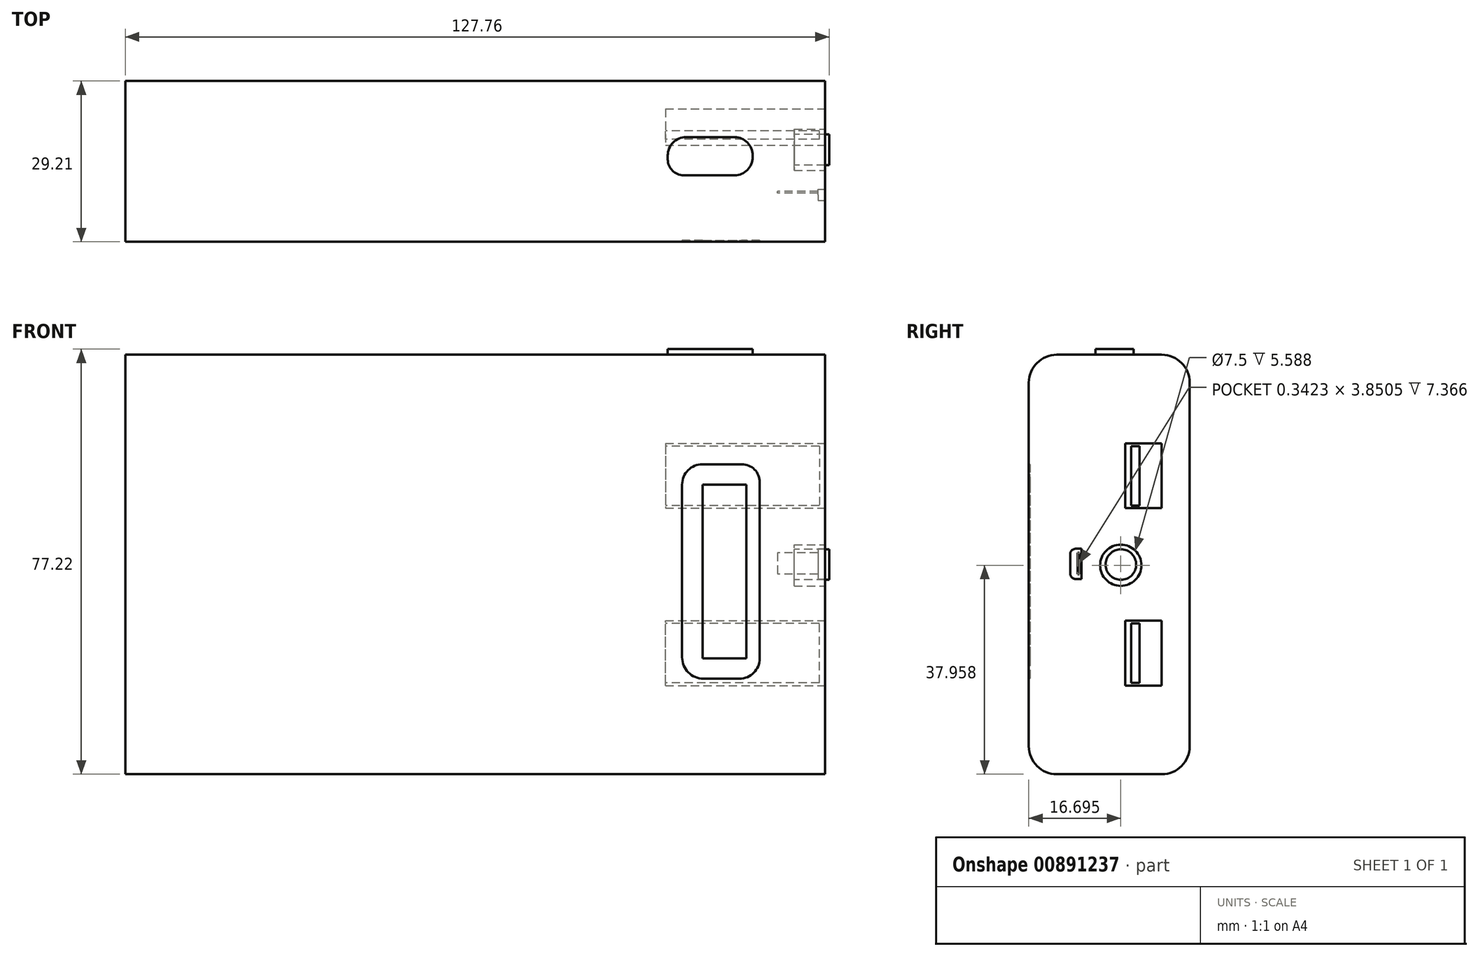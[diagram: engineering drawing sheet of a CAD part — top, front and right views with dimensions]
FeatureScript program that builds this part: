
annotation { "Feature Type Name" : "Feature", "Feature Type Description" : "" }
export const myFeature = defineFeature(function(context is Context, id is Id, definition is map)
    precondition{}
    {
        {
            var Q0;
            Q0=qCreatedBy(makeId("Front.planeOp"),FACE);
            var sketch = newSketch(context, id + "F0", { "sketchPlane" : qUnion([Q0])});
            skLineSegment(sketch, "E0.bottom", {"start": v(-63.5, 38.1) * mm, "end": v(63.5, 38.1) * mm});
            skLineSegment(sketch, "E0.top", {"start": v(-63.5, -38.1) * mm, "end": v(63.5, -38.1) * mm});
            skLineSegment(sketch, "E0.left", {"start": v(-63.5, 38.1) * mm, "end": v(-63.5, -38.1) * mm});
            skLineSegment(sketch, "E0.right", {"start": v(63.5, 38.1) * mm, "end": v(63.5, -38.1) * mm});
            skPoint(sketch, "E0.middle", {"position": v(0, 0) * mm});
            skSolve(sketch);
        }
        {
            var Q0;
            Q0=makeQuery(id+"F0.imprint","IMPRINT",FACE,{"disambiguationData":[TD([[makeQuery(id+"F0.imprint","IMPRINT",EDGE,{"derivedFrom":sQuery(id+"F0.wireOp",EDGE,"E0.bottom")}),-1.0]])]});
            extrude(context, id + "F1", {"entities" : qUnion([Q0]), "depth" : 29.2 * mm, "offsetDistance" : 25.4 * mm});
        }
        {
            var Q0;
            Q0=makeQuery(id+"F1.opExtrude","CAP_EDGE",EDGE,{"disambiguationData":[OSD([sQuery(id+"F0.wireOp",EDGE,"E0.bottom")])],"isStart":false});
            var Q1;
            Q1=makeQuery(id+"F1.opExtrude","CAP_EDGE",EDGE,{"disambiguationData":[OSD([sQuery(id+"F0.wireOp",EDGE,"E0.bottom")])],"isStart":true});
            var Q2;
            Q2=makeQuery(id+"F1.opExtrude","CAP_EDGE",EDGE,{"disambiguationData":[OSD([sQuery(id+"F0.wireOp",EDGE,"E0.top")])],"isStart":false});
            var Q3;
            Q3=makeQuery(id+"F1.opExtrude","CAP_EDGE",EDGE,{"disambiguationData":[OSD([sQuery(id+"F0.wireOp",EDGE,"E0.top")])],"isStart":true});
            fillet(context, id + "F2", {"entities" : qUnion([Q0, Q1, Q2, Q3]), "radius" : 5.08 * mm, "tangentPropagation" : true, "allowEdgeOverflow" : false});
        }
        {
            var Q0;
            Q0=makeQuery(id+"F1.opExtrude","SWEPT_FACE",FACE,{"disambiguationData":[OSD([sQuery(id+"F0.wireOp",EDGE,"E0.right")])]});
            var sketch = newSketch(context, id + "F3", { "sketchPlane" : qUnion([Q0])});
            skLineSegment(sketch, "E1.bottom", {"start": v(-5.08, 22.02) * mm, "end": v(-11.7, 22.02) * mm});
            skLineSegment(sketch, "E1.top", {"start": v(-5.08, 10.22) * mm, "end": v(-11.7, 10.22) * mm});
            skLineSegment(sketch, "E1.left", {"start": v(-5.08, 22.02) * mm, "end": v(-5.08, 10.22) * mm});
            skLineSegment(sketch, "E1.right", {"start": v(-11.7, 22.02) * mm, "end": v(-11.7, 10.22) * mm});
            skLineSegment(sketch, "E2.MirrorCS", {"start": v(-5.08, -22.02) * mm, "end": v(-11.7, -22.02) * mm});
            skLineSegment(sketch, "E3.MirrorCS", {"start": v(-5.08, -22.02) * mm, "end": v(-5.08, -10.22) * mm});
            skLineSegment(sketch, "E4.MirrorCS", {"start": v(-5.08, -10.22) * mm, "end": v(-11.7, -10.22) * mm});
            skLineSegment(sketch, "E5.MirrorCS", {"start": v(-11.7, -22.02) * mm, "end": v(-11.7, -10.22) * mm});
            skSolve(sketch);
        }
        {
            var Q0;
            Q0 = qSketchRegion(id + "F3", true);
            extrude(context, id + "F4", {"entities" : qUnion([Q0]), "operationType" : NewBodyOperationType.REMOVE, "oppositeDirection" : true, "depth" : 28.96 * mm, "offsetDistance" : 25.4 * mm});
        }
        {
            var Q0;
            Q0=makeQuery(id+"F4.boolean.opBoolean","COPY",FACE,{"derivedFrom":makeQuery(id+"F4.opExtrude","CAP_FACE",FACE,{"disambiguationData":[OSD([sQuery(id+"F3.wireOp",EDGE,"E1.bottom"),sQuery(id+"F3.wireOp",EDGE,"E1.top"),sQuery(id+"F3.wireOp",EDGE,"E1.left"),sQuery(id+"F3.wireOp",EDGE,"E1.right")])],"isStart":false})});
            var sketch = newSketch(context, id + "F5", { "sketchPlane" : qUnion([Q0])});
            skLineSegment(sketch, "E6.bottom", {"start": v(-10.61, 21.5) * mm, "end": v(-9.09, 21.5) * mm});
            skLineSegment(sketch, "E6.top", {"start": v(-10.61, 10.68) * mm, "end": v(-9.09, 10.68) * mm});
            skLineSegment(sketch, "E6.left", {"start": v(-10.61, 21.5) * mm, "end": v(-10.61, 10.68) * mm});
            skLineSegment(sketch, "E6.right", {"start": v(-9.09, 21.5) * mm, "end": v(-9.09, 10.68) * mm});
            skLineSegment(sketch, "E7.MirrorCS", {"start": v(-10.61, -21.5) * mm, "end": v(-10.61, -10.68) * mm});
            skLineSegment(sketch, "E8.MirrorCS", {"start": v(-9.09, -21.5) * mm, "end": v(-9.09, -10.68) * mm});
            skLineSegment(sketch, "E9.MirrorCS", {"start": v(-10.61, -10.68) * mm, "end": v(-9.09, -10.68) * mm});
            skLineSegment(sketch, "E10.MirrorCS", {"start": v(-10.61, -21.5) * mm, "end": v(-9.09, -21.5) * mm});
            skSolve(sketch);
        }
        {
            var Q0;
            Q0=makeQuery(id+"F5.imprint","IMPRINT",FACE,{"disambiguationData":[TD([[makeQuery(id+"F5.imprint","IMPRINT",EDGE,{"derivedFrom":sQuery(id+"F5.wireOp",EDGE,"E6.bottom")}),-1.0]])]});
            var Q1;
            Q1=makeQuery(id+"F5.imprint","IMPRINT",FACE,{"disambiguationData":[TD([[makeQuery(id+"F5.imprint","IMPRINT",EDGE,{"derivedFrom":sQuery(id+"F5.wireOp",EDGE,"E7.MirrorCS")}),-1.0]])]});
            extrude(context, id + "F6", {"entities" : qUnion([Q0, Q1]), "operationType" : NewBodyOperationType.ADD, "depth" : 27.94 * mm, "offsetDistance" : 25.4 * mm});
        }
        {
            var Q0;
            Q0=makeQuery(id+"F1.opExtrude","SWEPT_FACE",FACE,{"disambiguationData":[OSD([sQuery(id+"F0.wireOp",EDGE,"E0.right")])]});
            var sketch = newSketch(context, id + "F7", { "sketchPlane" : qUnion([Q0])});
            skCircle(sketch, "E11", {"center": v(-12.52, -0.14) * mm, "radius": 3.75 * mm});
            skPoint(sketch, "E11.first.point", {"position": v(-8.78, -0.43) * mm});
            skPoint(sketch, "E11.second.point", {"position": v(-16.26, 0) * mm});
            skPoint(sketch, "E11.third.point", {"position": v(-10.5, 3.02) * mm});
            skSolve(sketch);
        }
        {
            var Q0;
            Q0=makeQuery(id+"F7.imprint","IMPRINT",FACE,{"disambiguationData":[TD([[makeQuery(id+"F7.imprint","IMPRINT",EDGE,{"derivedFrom":sQuery(id+"F7.wireOp",EDGE,"E11")}),1.0]])]});
            extrude(context, id + "F8", {"entities" : qUnion([Q0]), "operationType" : NewBodyOperationType.REMOVE, "oppositeDirection" : true, "depth" : 5.6 * mm, "offsetDistance" : 25.4 * mm});
        }
        {
            var Q0;
            Q0=makeQuery(id+"F8.boolean.opBoolean","COPY",FACE,{"derivedFrom":makeQuery(id+"F8.opExtrude","CAP_FACE",FACE,{"disambiguationData":[OSD([sQuery(id+"F7.wireOp",EDGE,"E11")])],"isStart":false})});
            var sketch = newSketch(context, id + "F9", { "sketchPlane" : qUnion([Q0])});
            skCircle(sketch, "E12", {"center": v(-12.5, -0.02) * mm, "radius": 2.78 * mm});
            skPoint(sketch, "E12.first.point", {"position": v(-12.54, 2.76) * mm});
            skPoint(sketch, "E12.second.point", {"position": v(-12.54, -2.8) * mm});
            skPoint(sketch, "E12.third.point", {"position": v(-10.49, -1.94) * mm});
            skSolve(sketch);
        }
        {
            var Q0;
            Q0=makeQuery(id+"F9.imprint","IMPRINT",FACE,{"disambiguationData":[TD([[makeQuery(id+"F9.imprint","IMPRINT",EDGE,{"derivedFrom":sQuery(id+"F9.wireOp",EDGE,"E12")}),1.0]])]});
            extrude(context, id + "F10", {"entities" : qUnion([Q0]), "operationType" : NewBodyOperationType.ADD, "depth" : 6.35 * mm, "offsetDistance" : 25.4 * mm});
        }
        {
            var Q0;
            Q0=makeQuery(id+"F1.opExtrude","SWEPT_FACE",FACE,{"disambiguationData":[OSD([sQuery(id+"F0.wireOp",EDGE,"E0.right")])]});
            var sketch = newSketch(context, id + "F11", { "sketchPlane" : qUnion([Q0])});
            skLineSegment(sketch, "E13.bottom", {"start": v(-20.67, 2.86) * mm, "end": v(-19.66, 2.86) * mm});
            skLineSegment(sketch, "E13.top", {"start": v(-20.67, -2.65) * mm, "end": v(-19.66, -2.65) * mm});
            skLineSegment(sketch, "E13.left", {"start": v(-21.7, 1.83) * mm, "end": v(-21.7, -1.62) * mm});
            skLineSegment(sketch, "E13.right", {"start": v(-19.66, 2.86) * mm, "end": v(-19.66, -2.65) * mm});
            skPoint(sketch, "E14.visualSharp", {"position": v(-21.7, 2.86) * mm});
            skArc(sketch, "E14.filletArc", {"start": v(-20.67, 2.86) * mm, "mid": v(-21.4, 2.56) * mm, "end": v(-21.7, 1.83) * mm});
            skPoint(sketch, "E15.visualSharp", {"position": v(-21.7, -2.65) * mm});
            skArc(sketch, "E15.filletArc", {"start": v(-21.7, -1.62) * mm, "mid": v(-21.4, -2.35) * mm, "end": v(-20.67, -2.65) * mm});
            skSolve(sketch);
        }
        {
            var Q0;
            Q0=makeQuery(id+"F11.imprint","IMPRINT",FACE,{"disambiguationData":[TD([[makeQuery(id+"F11.imprint","IMPRINT",EDGE,{"derivedFrom":sQuery(id+"F11.wireOp",EDGE,"E13.bottom")}),-1.0]])]});
            extrude(context, id + "F12", {"entities" : qUnion([Q0]), "operationType" : NewBodyOperationType.REMOVE, "oppositeDirection" : true, "depth" : 8.64 * mm, "offsetDistance" : 25.4 * mm});
        }
        {
            var Q0;
            Q0=makeQuery(id+"F12.boolean.opBoolean","COPY",FACE,{"derivedFrom":makeQuery(id+"F12.opExtrude","CAP_FACE",FACE,{"disambiguationData":[OSD([sQuery(id+"F11.wireOp",EDGE,"E13.bottom"),sQuery(id+"F11.wireOp",EDGE,"E13.top"),sQuery(id+"F11.wireOp",EDGE,"E13.left"),sQuery(id+"F11.wireOp",EDGE,"E13.right"),sQuery(id+"F11.wireOp",EDGE,"E14.filletArc"),sQuery(id+"F11.wireOp",EDGE,"E15.filletArc")])],"isStart":false})});
            var sketch = newSketch(context, id + "F13", { "sketchPlane" : qUnion([Q0])});
            skLineSegment(sketch, "E16.bottom", {"start": v(-20.36, 2.12) * mm, "end": v(-20.02, 2.12) * mm});
            skLineSegment(sketch, "E16.top", {"start": v(-20.36, -1.73) * mm, "end": v(-20.02, -1.73) * mm});
            skLineSegment(sketch, "E16.left", {"start": v(-20.36, 2.12) * mm, "end": v(-20.36, -1.73) * mm});
            skLineSegment(sketch, "E16.right", {"start": v(-20.02, 2.12) * mm, "end": v(-20.02, -1.73) * mm});
            skLineSegment(sketch, "E17.bottom", {"start": v(-20.02, 1.3) * mm, "end": v(-20.36, 1.3) * mm});
            skLineSegment(sketch, "E17.top", {"start": v(-20.02, 0) * mm, "end": v(-20.36, 0) * mm});
            skLineSegment(sketch, "E17.left", {"start": v(-20.02, 1.3) * mm, "end": v(-20.02, 0) * mm});
            skLineSegment(sketch, "E17.right", {"start": v(-20.36, 1.3) * mm, "end": v(-20.36, 0) * mm});
            skSolve(sketch);
        }
        {
            var Q0;
            {var subQ5=sQuery(id+"F13.wireOp",EDGE,"E16.bottom");Q0=makeQuery(id+"F13.imprint","IMPRINT",FACE,{"disambiguationData":[TD([[makeQuery(id+"F13.imprint","IMPRINT",EDGE,{"derivedFrom":subQ5}),1.0]])]});}
            extrude(context, id + "F14", {"entities" : qUnion([Q0]), "operationType" : NewBodyOperationType.ADD, "depth" : 7.37 * mm, "offsetDistance" : 25.4 * mm});
        }
        {
            var Q0;
            Q0=makeQuery(id+"F1.opExtrude","SWEPT_FACE",FACE,{"disambiguationData":[OSD([sQuery(id+"F0.wireOp",EDGE,"E0.bottom")])]});
            var sketch = newSketch(context, id + "F15", { "sketchPlane" : qUnion([Q0])});
            skLineSegment(sketch, "E18.bottom", {"start": v(38.27, -10.22) * mm, "end": v(47.09, -10.22) * mm});
            skLineSegment(sketch, "E18.top", {"start": v(37.85, -17.12) * mm, "end": v(47.09, -17.12) * mm});
            skLineSegment(sketch, "E18.left", {"start": v(34.97, -13.52) * mm, "end": v(34.97, -14.25) * mm});
            skLineSegment(sketch, "E18.right", {"start": v(50.39, -13.52) * mm, "end": v(50.39, -13.82) * mm});
            skPoint(sketch, "E19.visualSharp", {"position": v(34.97, -10.22) * mm});
            skArc(sketch, "E19.filletArc", {"start": v(38.27, -10.22) * mm, "mid": v(35.94, -11.18) * mm, "end": v(34.97, -13.52) * mm});
            skPoint(sketch, "E20.visualSharp", {"position": v(34.97, -17.12) * mm});
            skArc(sketch, "E20.filletArc", {"start": v(34.97, -14.25) * mm, "mid": v(35.81, -16.28) * mm, "end": v(37.85, -17.12) * mm});
            skPoint(sketch, "E21.visualSharp", {"position": v(50.39, -10.22) * mm});
            skArc(sketch, "E21.filletArc", {"start": v(50.39, -13.52) * mm, "mid": v(49.42, -11.18) * mm, "end": v(47.09, -10.22) * mm});
            skPoint(sketch, "E22.visualSharp", {"position": v(50.39, -17.12) * mm});
            skArc(sketch, "E22.filletArc", {"start": v(47.09, -17.12) * mm, "mid": v(49.42, -16.16) * mm, "end": v(50.39, -13.82) * mm});
            skSolve(sketch);
        }
        {
            var Q0;
            Q0=makeQuery(id+"F15.imprint","IMPRINT",FACE,{"disambiguationData":[TD([[makeQuery(id+"F15.imprint","IMPRINT",EDGE,{"derivedFrom":sQuery(id+"F15.wireOp",EDGE,"E18.bottom")}),-1.0]])]});
            extrude(context, id + "F16", {"entities" : qUnion([Q0]), "operationType" : NewBodyOperationType.REMOVE, "oppositeDirection" : true, "depth" : 3.56 * mm, "offsetDistance" : 25.4 * mm});
        }
        {
            var Q0;
            Q0=makeQuery(id+"F16.boolean.opBoolean","COPY",FACE,{"derivedFrom":makeQuery(id+"F16.opExtrude","CAP_FACE",FACE,{"disambiguationData":[OSD([sQuery(id+"F15.wireOp",EDGE,"E18.bottom"),sQuery(id+"F15.wireOp",EDGE,"E18.top"),sQuery(id+"F15.wireOp",EDGE,"E18.left"),sQuery(id+"F15.wireOp",EDGE,"E18.right"),sQuery(id+"F15.wireOp",EDGE,"E19.filletArc"),sQuery(id+"F15.wireOp",EDGE,"E20.filletArc"),sQuery(id+"F15.wireOp",EDGE,"E21.filletArc"),sQuery(id+"F15.wireOp",EDGE,"E22.filletArc")])],"isStart":false})});
            extrude(context, id + "F17", {"entities" : qUnion([Q0]), "operationType" : NewBodyOperationType.ADD, "depth" : 4.57 * mm, "offsetDistance" : 25.4 * mm});
        }
        {
            var Q0;
            Q0=makeQuery(id+"F1.opExtrude","CAP_FACE",FACE,{"disambiguationData":[OSD([sQuery(id+"F0.wireOp",EDGE,"E0.bottom"),sQuery(id+"F0.wireOp",EDGE,"E0.top"),sQuery(id+"F0.wireOp",EDGE,"E0.left"),sQuery(id+"F0.wireOp",EDGE,"E0.right")])],"isStart":false});
            var sketch = newSketch(context, id + "F18", { "sketchPlane" : qUnion([Q0])});
            skLineSegment(sketch, "E23.bottom", {"start": v(41.26, 18.22) * mm, "end": v(48.37, 18.22) * mm});
            skLineSegment(sketch, "E23.top", {"start": v(41.46, -20.75) * mm, "end": v(47.98, -20.75) * mm});
            skLineSegment(sketch, "E23.left", {"start": v(37.57, 14.52) * mm, "end": v(37.57, -16.86) * mm});
            skLineSegment(sketch, "E23.right", {"start": v(51.67, 14.92) * mm, "end": v(51.67, -17.06) * mm});
            skPoint(sketch, "E24.visualSharp", {"position": v(37.57, 18.22) * mm});
            skArc(sketch, "E24.filletArc", {"start": v(41.26, 18.22) * mm, "mid": v(38.65, 17.13) * mm, "end": v(37.57, 14.52) * mm});
            skPoint(sketch, "E25.visualSharp", {"position": v(51.67, 18.22) * mm});
            skArc(sketch, "E25.filletArc", {"start": v(51.67, 14.92) * mm, "mid": v(50.7, 17.25) * mm, "end": v(48.37, 18.22) * mm});
            skPoint(sketch, "E26.visualSharp", {"position": v(37.57, -20.75) * mm});
            skArc(sketch, "E26.filletArc", {"start": v(37.57, -16.86) * mm, "mid": v(38.7, -19.61) * mm, "end": v(41.46, -20.75) * mm});
            skPoint(sketch, "E27.visualSharp", {"position": v(51.67, -20.75) * mm});
            skArc(sketch, "E27.filletArc", {"start": v(47.98, -20.75) * mm, "mid": v(50.59, -19.67) * mm, "end": v(51.67, -17.06) * mm});
            skLineSegment(sketch, "E28.bottom", {"start": v(41.26, 14.52) * mm, "end": v(49.25, 14.52) * mm});
            skLineSegment(sketch, "E28.top", {"start": v(41.26, -17.06) * mm, "end": v(49.25, -17.06) * mm});
            skLineSegment(sketch, "E28.left", {"start": v(41.26, 14.52) * mm, "end": v(41.26, -17.06) * mm});
            skLineSegment(sketch, "E28.right", {"start": v(49.25, 14.52) * mm, "end": v(49.25, -17.06) * mm});
            skSolve(sketch);
        }
        {
            var Q0;
            Q0=makeQuery(id+"F18.imprint","IMPRINT",FACE,{"disambiguationData":[TD([[makeQuery(id+"F18.imprint","IMPRINT",EDGE,{"derivedFrom":sQuery(id+"F18.wireOp",EDGE,"E23.bottom")}),-1.0]])]});
            extrude(context, id + "F19", {"entities" : qUnion([Q0]), "operationType" : NewBodyOperationType.REMOVE, "oppositeDirection" : true, "depth" : 0.25 * mm, "offsetDistance" : 25.4 * mm});
        }
    });
